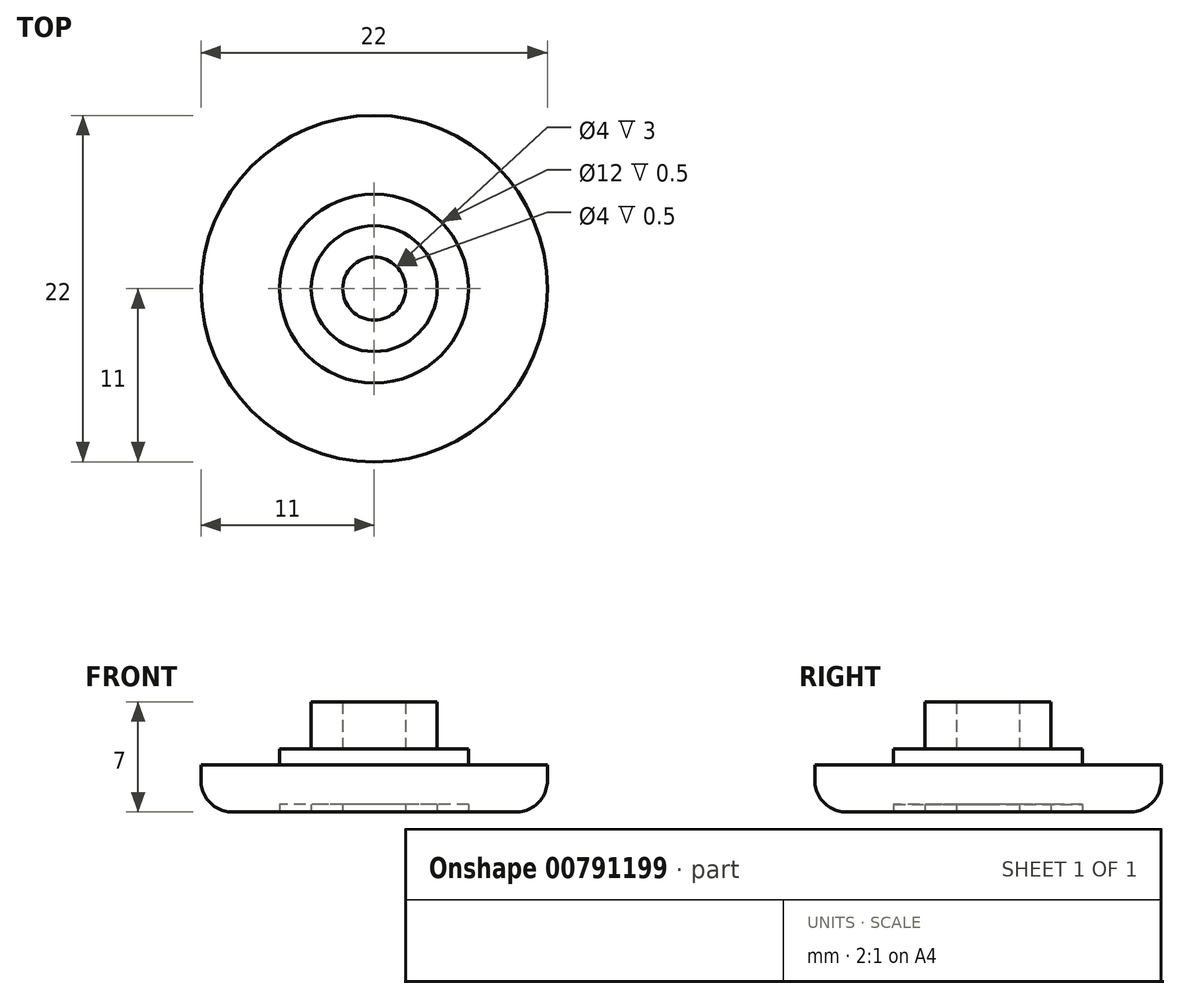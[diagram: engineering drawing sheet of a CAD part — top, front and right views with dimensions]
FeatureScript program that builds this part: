
annotation { "Feature Type Name" : "Feature", "Feature Type Description" : "" }
export const myFeature = defineFeature(function(context is Context, id is Id, definition is map)
    precondition{}
    {
        {
            var Q0;
            Q0=qCreatedBy(makeId("Top.planeOp"),FACE);
            var sketch = newSketch(context, id + "F0", { "sketchPlane" : qUnion([Q0])});
            skCircle(sketch, "E0", {"center": v(0, 0) * mm, "radius": 11 * mm});
            skCircle(sketch, "E1", {"center": v(0, 0) * mm, "radius": 6 * mm});
            skCircle(sketch, "E2", {"center": v(0, 0) * mm, "radius": 4 * mm});
            skCircle(sketch, "E3", {"center": v(0, 0) * mm, "radius": 2 * mm});
            skSolve(sketch);
        }
        {
            var Q0;
            Q0=makeQuery(id+"F0.imprint","IMPRINT",FACE,{"disambiguationData":[TD([[makeQuery(id+"F0.imprint","IMPRINT",EDGE,{"derivedFrom":sQuery(id+"F0.wireOp",EDGE,"E2")}),1.0]])]});
            extrude(context, id + "F1", {"entities" : qUnion([Q0]), "depth" : 7 * mm, "offsetDistance" : 25 * mm});
        }
        {
            var Q0;
            Q0=makeQuery(id+"F0.imprint","IMPRINT",FACE,{"disambiguationData":[TD([[makeQuery(id+"F0.imprint","IMPRINT",EDGE,{"derivedFrom":sQuery(id+"F0.wireOp",EDGE,"E1")}),1.0]])]});
            extrude(context, id + "F2", {"entities" : qUnion([Q0]), "operationType" : NewBodyOperationType.ADD, "depth" : 4 * mm, "offsetDistance" : 25 * mm});
        }
        {
            var Q0;
            Q0=makeQuery(id+"F0.imprint","IMPRINT",FACE,{"disambiguationData":[TD([[makeQuery(id+"F0.imprint","IMPRINT",EDGE,{"derivedFrom":sQuery(id+"F0.wireOp",EDGE,"E0")}),1.0]])]});
            extrude(context, id + "F3", {"entities" : qUnion([Q0]), "operationType" : NewBodyOperationType.ADD, "depth" : 3 * mm, "offsetDistance" : 25 * mm});
        }
        {
            var Q0;
            Q0=makeQuery(id+"F0.imprint","IMPRINT",FACE,{"disambiguationData":[TD([[makeQuery(id+"F0.imprint","IMPRINT",EDGE,{"derivedFrom":sQuery(id+"F0.wireOp",EDGE,"E3")}),1.0]])]});
            extrude(context, id + "F4", {"entities" : qUnion([Q0]), "operationType" : NewBodyOperationType.ADD, "depth" : 4 * mm, "offsetDistance" : 25 * mm});
        }
        {
            var Q0;
            Q0=makeQuery(id+"F3.opExtrude","CAP_EDGE",EDGE,{"disambiguationData":[OSD([sQuery(id+"F0.wireOp",EDGE,"E0")])],"isStart":true});
            fillet(context, id + "F5", {"entities" : qUnion([Q0]), "radius" : 2 * mm, "tangentPropagation" : true, "allowEdgeOverflow" : false});
        }
        {
            var Q0;
            Q0=makeQuery(id+"F0.imprint","IMPRINT",FACE,{"disambiguationData":[TD([[makeQuery(id+"F0.imprint","IMPRINT",EDGE,{"derivedFrom":sQuery(id+"F0.wireOp",EDGE,"E1")}),1.0]])]});
            var Q1;
            Q1=makeQuery(id+"F0.imprint","IMPRINT",FACE,{"disambiguationData":[TD([[makeQuery(id+"F0.imprint","IMPRINT",EDGE,{"derivedFrom":sQuery(id+"F0.wireOp",EDGE,"E3")}),1.0]])]});
            extrude(context, id + "F6", {"entities" : qUnion([Q0, Q1]), "operationType" : NewBodyOperationType.REMOVE, "depth" : 0.5 * mm, "offsetDistance" : 25 * mm});
        }
    });
